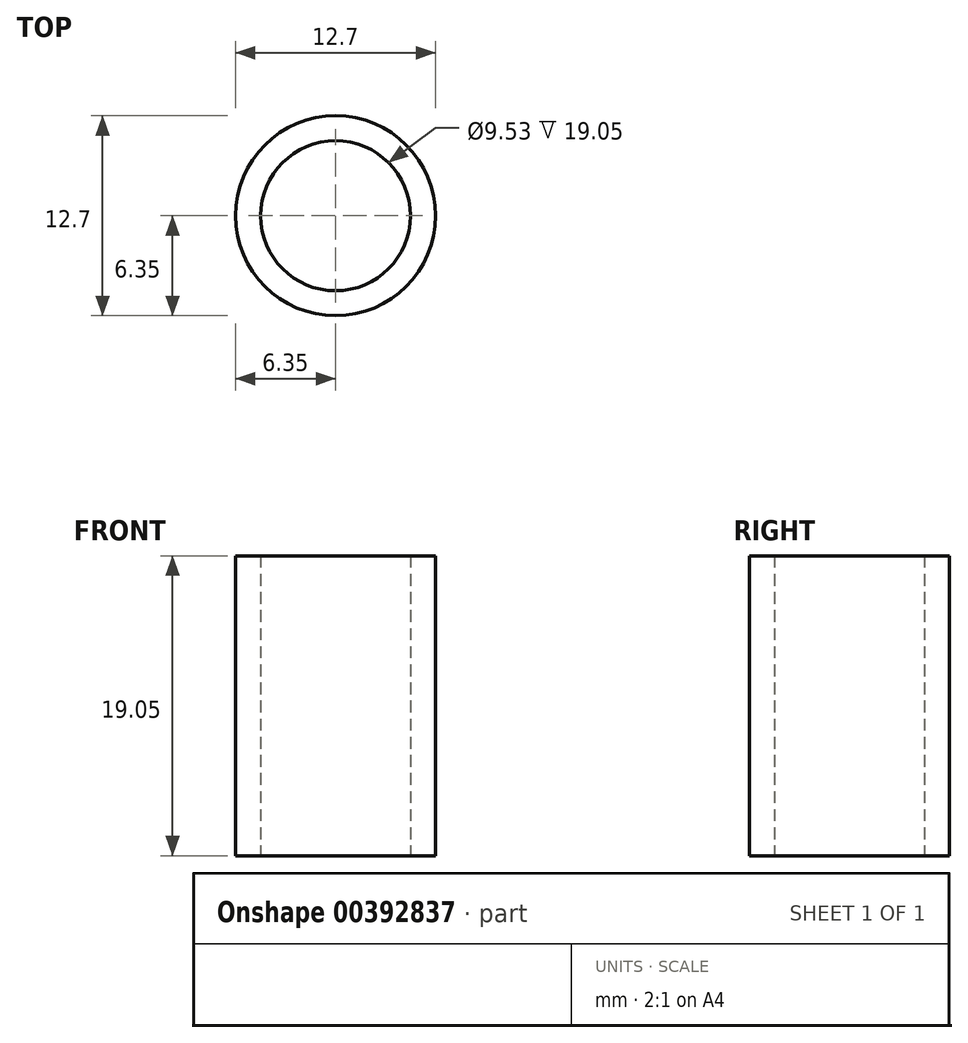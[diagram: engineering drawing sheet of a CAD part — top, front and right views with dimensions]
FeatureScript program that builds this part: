
annotation { "Feature Type Name" : "Feature", "Feature Type Description" : "" }
export const myFeature = defineFeature(function(context is Context, id is Id, definition is map)
    precondition{}
    {
        {
            var Q0;
            Q0=qCreatedBy(makeId("Top.planeOp"),FACE);
            var sketch = newSketch(context, id + "F0", { "sketchPlane" : qUnion([Q0])});
            skCircle(sketch, "E0", {"center": v(0, 0) * mm, "radius": 6.35 * mm});
            skCircle(sketch, "E1", {"center": v(0, 0) * mm, "radius": 4.76 * mm});
            skSolve(sketch);
        }
        {
            var Q0;
            Q0 = qSketchRegion(id + "F0", true);
            extrude(context, id + "F1", {"entities" : qUnion([Q0]), "depth" : 19.05 * mm});
        }
    });
